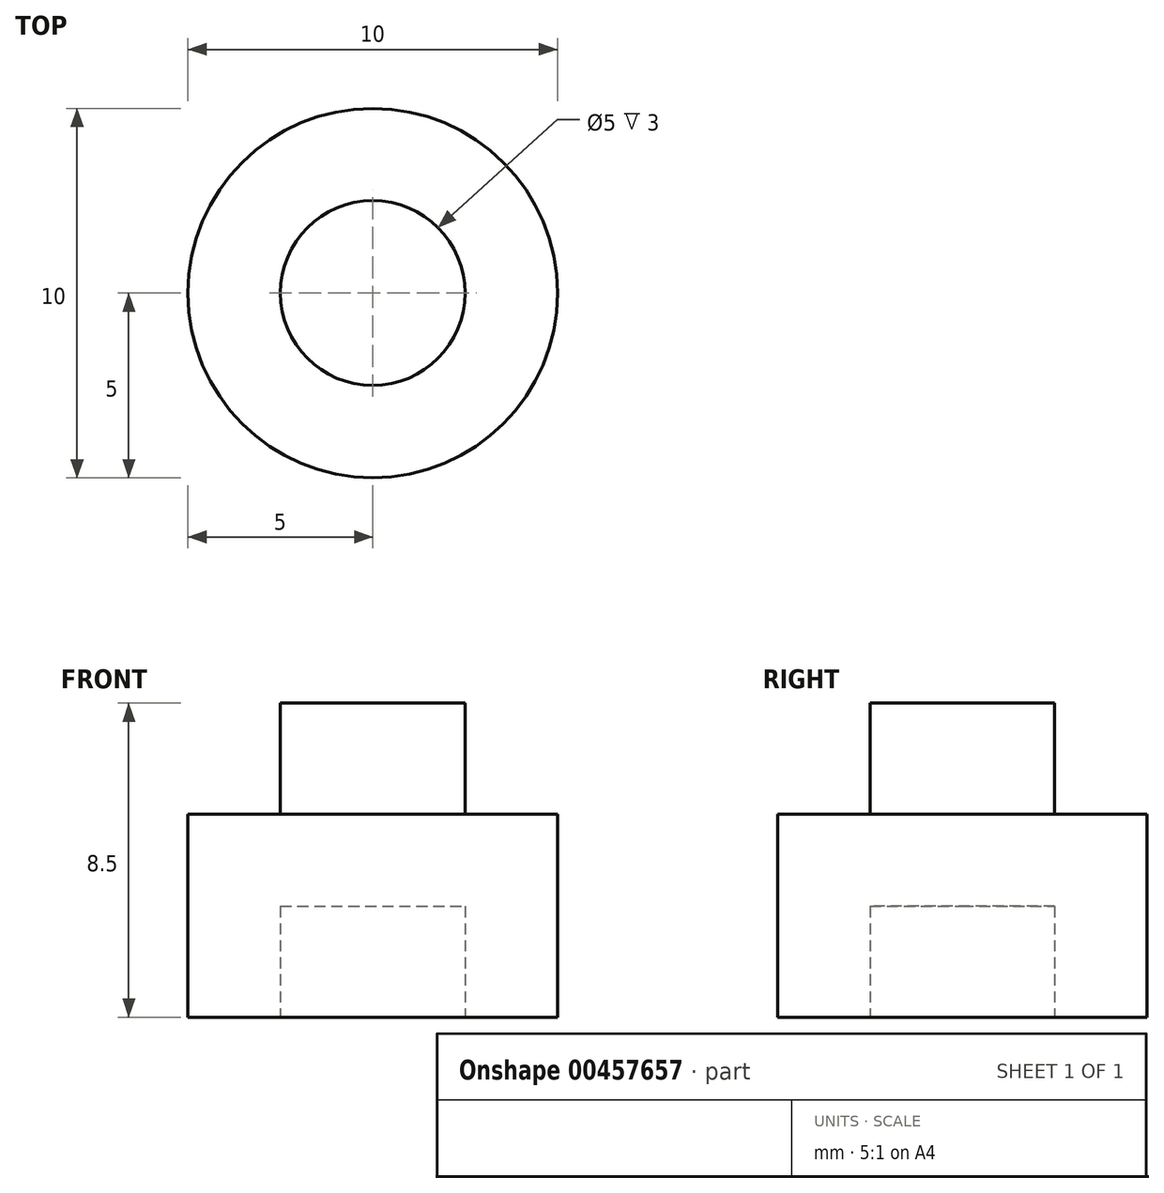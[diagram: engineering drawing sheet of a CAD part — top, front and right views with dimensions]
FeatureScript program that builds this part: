
annotation { "Feature Type Name" : "Feature", "Feature Type Description" : "" }
export const myFeature = defineFeature(function(context is Context, id is Id, definition is map)
    precondition{}
    {
        {
            var Q0;
            Q0=qCreatedBy(makeId("Front.planeOp"),FACE);
            var sketch = newSketch(context, id + "F0", { "sketchPlane" : qUnion([Q0])});
            skLineSegment(sketch, "E0", {"start": v(-2.5, 0) * mm, "end": v(-2.5, 3) * mm});
            skLineSegment(sketch, "E1", {"start": v(-2.5, 3) * mm, "end": v(0, 3) * mm});
            skLineSegment(sketch, "E2", {"start": v(0, 3) * mm, "end": v(0, 8.5) * mm});
            skLineSegment(sketch, "E3", {"start": v(0, 8.5) * mm, "end": v(-2.5, 8.5) * mm});
            skLineSegment(sketch, "E4", {"start": v(-2.5, 8.5) * mm, "end": v(-2.5, 5.5) * mm});
            skLineSegment(sketch, "E5", {"start": v(-2.5, 5.5) * mm, "end": v(-5, 5.5) * mm});
            skLineSegment(sketch, "E6", {"start": v(-5, 5.5) * mm, "end": v(-5, 0) * mm});
            skLineSegment(sketch, "E7", {"start": v(-5, 0) * mm, "end": v(-2.5, 0) * mm});
            skSolve(sketch);
        }
        {
            var Q0;
            Q0=makeQuery(id+"F0.imprint","IMPRINT",FACE,{"disambiguationData":[TD([[makeQuery(id+"F0.imprint","IMPRINT",EDGE,{"derivedFrom":sQuery(id+"F0.wireOp",EDGE,"E0")}),1.0]])]});
            var Q1;
            Q1=sQuery(id+"F0.wireOp",EDGE,"E2");
            revolve(context, id + "F1", {"entities" : qUnion([Q0]), "axis" : qUnion([Q1]), "revolveType" : RevolveType.FULL});
        }
    });
